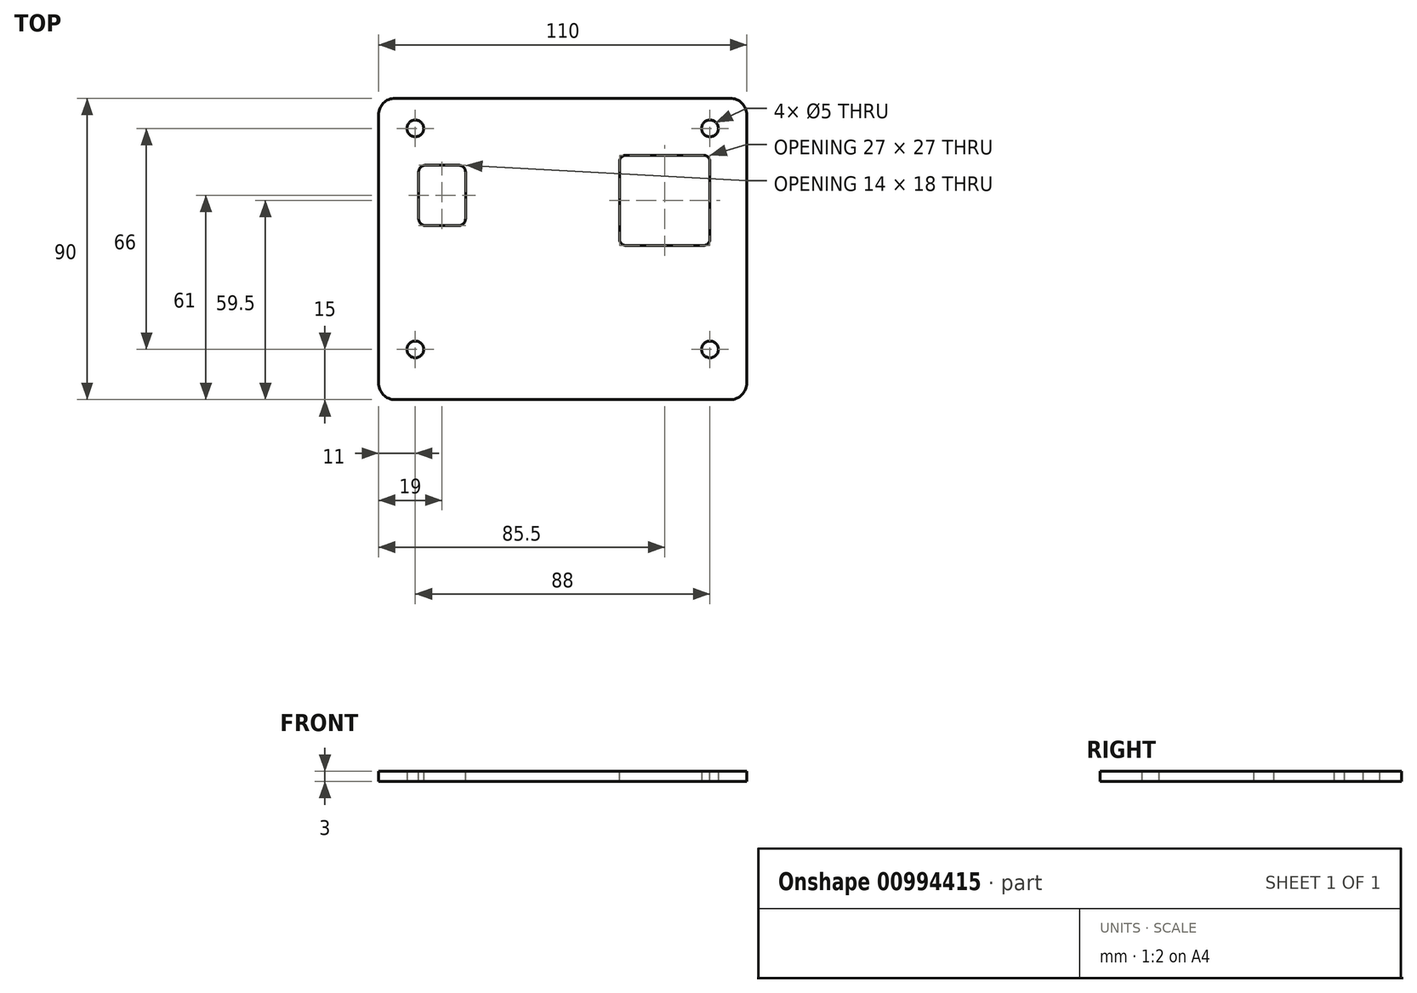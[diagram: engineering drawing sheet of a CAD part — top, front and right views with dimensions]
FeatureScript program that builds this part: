
annotation { "Feature Type Name" : "Feature", "Feature Type Description" : "" }
export const myFeature = defineFeature(function(context is Context, id is Id, definition is map)
    precondition{}
    {
        {
            var Q0;
            Q0=qCreatedBy(makeId("Top.planeOp"),FACE);
            var sketch = newSketch(context, id + "F0", { "sketchPlane" : qUnion([Q0])});
            skLineSegment(sketch, "E0.bottom", {"start": v(55, -45) * mm, "end": v(-55, -45) * mm});
            skLineSegment(sketch, "E0.top", {"start": v(55, 45) * mm, "end": v(-55, 45) * mm});
            skLineSegment(sketch, "E0.left", {"start": v(55, -45) * mm, "end": v(55, 45) * mm});
            skLineSegment(sketch, "E0.right", {"start": v(-55, -45) * mm, "end": v(-55, 45) * mm});
            skPoint(sketch, "E0.middle", {"position": v(0, 0) * mm});
            skSolve(sketch);
        }
        {
            var Q0;
            Q0=makeQuery(id+"F0.imprint","IMPRINT",FACE,{"disambiguationData":[TD([[makeQuery(id+"F0.imprint","IMPRINT",EDGE,{"derivedFrom":sQuery(id+"F0.wireOp",EDGE,"E0.bottom")}),-1.0]])]});
            extrude(context, id + "F1", {"entities" : qUnion([Q0]), "depth" : 3 * mm, "offsetDistance" : 25 * mm});
        }
        {
            var Q0;
            Q0=makeQuery(id+"F1.opExtrude","SWEPT_EDGE",EDGE,{"disambiguationData":[OSD([sQuery(id+"F0.wireOp",EDGE,"E0.top"),sQuery(id+"F0.wireOp",EDGE,"E0.left")])]});
            var Q1;
            Q1=makeQuery(id+"F1.opExtrude","SWEPT_EDGE",EDGE,{"disambiguationData":[OSD([sQuery(id+"F0.wireOp",EDGE,"E0.bottom"),sQuery(id+"F0.wireOp",EDGE,"E0.left")])]});
            var Q2;
            Q2=makeQuery(id+"F1.opExtrude","SWEPT_EDGE",EDGE,{"disambiguationData":[OSD([sQuery(id+"F0.wireOp",EDGE,"E0.top"),sQuery(id+"F0.wireOp",EDGE,"E0.right")])]});
            var Q3;
            Q3=makeQuery(id+"F1.opExtrude","SWEPT_EDGE",EDGE,{"disambiguationData":[OSD([sQuery(id+"F0.wireOp",EDGE,"E0.bottom"),sQuery(id+"F0.wireOp",EDGE,"E0.right")])]});
            fillet(context, id + "F2", {"entities" : qUnion([Q0, Q1, Q2, Q3]), "radius" : 5 * mm, "tangentPropagation" : true, "allowEdgeOverflow" : false});
        }
        {
            var Q0;
            Q0=qCreatedBy(makeId("Top.planeOp"),FACE);
            var sketch = newSketch(context, id + "F3", { "sketchPlane" : qUnion([Q0])});
            skPoint(sketch, "E1", {"position": v(-22, -37) * mm});
            skPoint(sketch, "E2", {"position": v(-9.3, -37) * mm});
            skPoint(sketch, "E3", {"position": v(3.4, -37) * mm});
            skPoint(sketch, "E4", {"position": v(-44, 36) * mm});
            skPoint(sketch, "E5", {"position": v(44, 36) * mm});
            skPoint(sketch, "E6", {"position": v(-44, -30) * mm});
            skPoint(sketch, "E7", {"position": v(44, -30) * mm});
            skSolve(sketch);
        }
        {
            var Q0;
            Q0=sQuery(id+"F3.wireOp",VERTEX,"E4");
            var Q1;
            Q1=sQuery(id+"F3.wireOp",VERTEX,"E5");
            var Q2;
            Q2=makeQuery(id+"F1.opExtrude","SWEPT_BODY",BODY,{"disambiguationData":[OSD([sQuery(id+"F0.wireOp",EDGE,"E0.bottom"),sQuery(id+"F0.wireOp",EDGE,"E0.top"),sQuery(id+"F0.wireOp",EDGE,"E0.left"),sQuery(id+"F0.wireOp",EDGE,"E0.right")])]});
            hole(context, id + "F4", {"style" : HoleStyle.SIMPLE, "endStyle" : HoleEndStyle.THROUGH, "oppositeDirection" : true, "holeDiameter" : 5 * mm, "majorDiameter" : 5 * mm, "isTappedThrough" : true, "tappedDepth" : 12 * mm, "tapClearance" : 3, "locations" : qUnion([Q0, Q1]), "scope" : qUnion([Q2])});
        }
        {
            var Q0;
            Q0=sQuery(id+"F3.wireOp",VERTEX,"E6");
            var Q1;
            Q1=sQuery(id+"F3.wireOp",VERTEX,"E7");
            var Q2;
            Q2=makeQuery(id+"F1.opExtrude","SWEPT_BODY",BODY,{"disambiguationData":[OSD([sQuery(id+"F0.wireOp",EDGE,"E0.bottom"),sQuery(id+"F0.wireOp",EDGE,"E0.top"),sQuery(id+"F0.wireOp",EDGE,"E0.left"),sQuery(id+"F0.wireOp",EDGE,"E0.right")])]});
            hole(context, id + "F5", {"style" : HoleStyle.SIMPLE, "endStyle" : HoleEndStyle.THROUGH, "oppositeDirection" : true, "holeDiameter" : 5 * mm, "majorDiameter" : 5 * mm, "isTappedThrough" : true, "tappedDepth" : 12 * mm, "tapClearance" : 3, "locations" : qUnion([Q0, Q1]), "scope" : qUnion([Q2])});
        }
        {
            var Q0;
            Q0=makeQuery(id+"F1.opExtrude","CAP_FACE",FACE,{"disambiguationData":[OSD([sQuery(id+"F0.wireOp",EDGE,"E0.bottom"),sQuery(id+"F0.wireOp",EDGE,"E0.top"),sQuery(id+"F0.wireOp",EDGE,"E0.left"),sQuery(id+"F0.wireOp",EDGE,"E0.right")])],"isStart":false});
            var sketch = newSketch(context, id + "F6", { "sketchPlane" : qUnion([Q0])});
            skLineSegment(sketch, "E8.bottom", {"start": v(-43, 25) * mm, "end": v(-29, 25) * mm});
            skLineSegment(sketch, "E8.top", {"start": v(-43, 7) * mm, "end": v(-29, 7) * mm});
            skLineSegment(sketch, "E8.left", {"start": v(-43, 25) * mm, "end": v(-43, 7) * mm});
            skLineSegment(sketch, "E8.right", {"start": v(-29, 25) * mm, "end": v(-29, 7) * mm});
            skLineSegment(sketch, "E9.bottom", {"start": v(17, 28) * mm, "end": v(44, 28) * mm});
            skLineSegment(sketch, "E9.top", {"start": v(17, 1) * mm, "end": v(44, 1) * mm});
            skLineSegment(sketch, "E9.left", {"start": v(17, 28) * mm, "end": v(17, 1) * mm});
            skLineSegment(sketch, "E9.right", {"start": v(44, 28) * mm, "end": v(44, 1) * mm});
            skSolve(sketch);
        }
        {
            var Q0;
            Q0=makeQuery(id+"F6.imprint","IMPRINT",FACE,{"disambiguationData":[TD([[makeQuery(id+"F6.imprint","IMPRINT",EDGE,{"derivedFrom":sQuery(id+"F6.wireOp",EDGE,"E8.bottom")}),-1.0]])]});
            var Q1;
            Q1=makeQuery(id+"F6.imprint","IMPRINT",FACE,{"disambiguationData":[TD([[makeQuery(id+"F6.imprint","IMPRINT",EDGE,{"derivedFrom":sQuery(id+"F6.wireOp",EDGE,"E9.bottom")}),-1.0]])]});
            extrude(context, id + "F7", {"entities" : qUnion([Q0, Q1]), "operationType" : NewBodyOperationType.REMOVE, "endBound" : BoundingType.THROUGH_ALL, "oppositeDirection" : true, "depth" : 25 * mm, "offsetDistance" : 25 * mm});
        }
        {
            var Q0;
            Q0=makeQuery(id+"F7.boolean.opBoolean","COPY",EDGE,{"derivedFrom":makeQuery(id+"F7.opExtrude","SWEPT_EDGE",EDGE,{"disambiguationData":[OSD([sQuery(id+"F6.wireOp",EDGE,"E8.top"),sQuery(id+"F6.wireOp",EDGE,"E8.left")])]})});
            var Q1;
            Q1=makeQuery(id+"F7.boolean.opBoolean","COPY",EDGE,{"derivedFrom":makeQuery(id+"F7.opExtrude","SWEPT_EDGE",EDGE,{"disambiguationData":[OSD([sQuery(id+"F6.wireOp",EDGE,"E9.top"),sQuery(id+"F6.wireOp",EDGE,"E9.left")])]})});
            var Q2;
            Q2=makeQuery(id+"F7.boolean.opBoolean","COPY",EDGE,{"derivedFrom":makeQuery(id+"F7.opExtrude","SWEPT_EDGE",EDGE,{"disambiguationData":[OSD([sQuery(id+"F6.wireOp",EDGE,"E8.top"),sQuery(id+"F6.wireOp",EDGE,"E8.right")])]})});
            var Q3;
            Q3=makeQuery(id+"F7.boolean.opBoolean","COPY",EDGE,{"derivedFrom":makeQuery(id+"F7.opExtrude","SWEPT_EDGE",EDGE,{"disambiguationData":[OSD([sQuery(id+"F6.wireOp",EDGE,"E8.bottom"),sQuery(id+"F6.wireOp",EDGE,"E8.left")])]})});
            var Q4;
            Q4=makeQuery(id+"F7.boolean.opBoolean","COPY",EDGE,{"derivedFrom":makeQuery(id+"F7.opExtrude","SWEPT_EDGE",EDGE,{"disambiguationData":[OSD([sQuery(id+"F6.wireOp",EDGE,"E9.bottom"),sQuery(id+"F6.wireOp",EDGE,"E9.left")])]})});
            var Q5;
            Q5=makeQuery(id+"F7.boolean.opBoolean","COPY",EDGE,{"derivedFrom":makeQuery(id+"F7.opExtrude","SWEPT_EDGE",EDGE,{"disambiguationData":[OSD([sQuery(id+"F6.wireOp",EDGE,"E9.bottom"),sQuery(id+"F6.wireOp",EDGE,"E9.right")])]})});
            var Q6;
            Q6=makeQuery(id+"F7.boolean.opBoolean","COPY",EDGE,{"derivedFrom":makeQuery(id+"F7.opExtrude","SWEPT_EDGE",EDGE,{"disambiguationData":[OSD([sQuery(id+"F6.wireOp",EDGE,"E9.top"),sQuery(id+"F6.wireOp",EDGE,"E9.right")])]})});
            var Q7;
            Q7=makeQuery(id+"F7.boolean.opBoolean","COPY",EDGE,{"derivedFrom":makeQuery(id+"F7.opExtrude","SWEPT_EDGE",EDGE,{"disambiguationData":[OSD([sQuery(id+"F6.wireOp",EDGE,"E8.bottom"),sQuery(id+"F6.wireOp",EDGE,"E8.right")])]})});
            fillet(context, id + "F8", {"entities" : qUnion([Q0, Q1, Q2, Q3, Q4, Q5, Q6, Q7]), "radius" : 2 * mm, "tangentPropagation" : true, "allowEdgeOverflow" : false});
        }
    });
